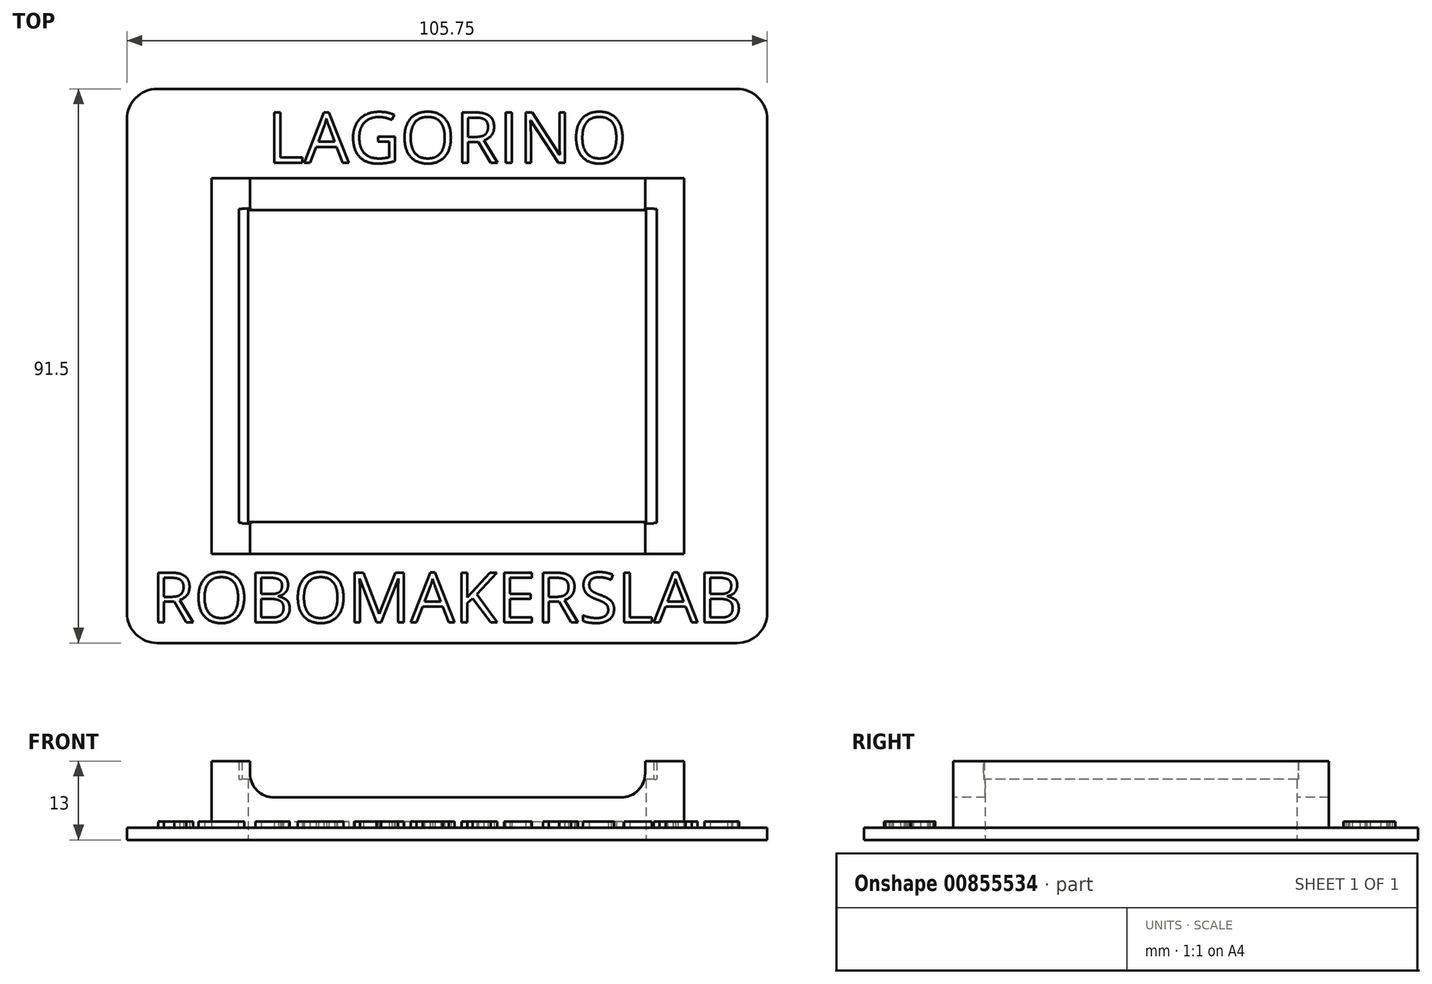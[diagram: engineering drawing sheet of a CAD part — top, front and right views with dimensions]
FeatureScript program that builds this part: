
annotation { "Feature Type Name" : "Feature", "Feature Type Description" : "" }
export const myFeature = defineFeature(function(context is Context, id is Id, definition is map)
    precondition{}
    {
        {
            var Q0;
            Q0=qCreatedBy(makeId("Top.planeOp"),FACE);
            var sketch = newSketch(context, id + "F0", { "sketchPlane" : qUnion([Q0])});
            skLineSegment(sketch, "E0.bottom", {"start": v(-39, 31) * mm, "end": v(39, 31) * mm});
            skLineSegment(sketch, "E0.top", {"start": v(-39, -31) * mm, "end": v(39, -31) * mm});
            skLineSegment(sketch, "E0.left", {"start": v(-39, 31) * mm, "end": v(-39, -31) * mm});
            skLineSegment(sketch, "E0.right", {"start": v(39, 31) * mm, "end": v(39, -31) * mm});
            skPoint(sketch, "E0.middle", {"position": v(0, 0) * mm});
            skLineSegment(sketch, "E1.0", {"start": v(-39, 25.75) * mm, "end": v(39, 25.75) * mm});
            skLineSegment(sketch, "E2.0", {"start": v(-39, -25.75) * mm, "end": v(39, -25.75) * mm});
            skLineSegment(sketch, "E3.0", {"start": v(-33, 31) * mm, "end": v(-33, -31) * mm});
            skLineSegment(sketch, "E4.0", {"start": v(32.75, 31) * mm, "end": v(32.75, -31) * mm});
            skSolve(sketch);
        }
        {
            var Q0;
            Q0 = qSketchRegion(id + "F0", true);
            extrude(context, id + "F1", {"entities" : qUnion([Q0]), "depth" : 10 * mm, "offsetDistance" : 25 * mm});
        }
        {
            var Q0;
            Q0=makeQuery(id+"F1.opExtrude","CAP_FACE",FACE,{"disambiguationData":[OSD([sQuery(id+"F0.wireOp",EDGE,"E0.bottom"),sQuery(id+"F0.wireOp",EDGE,"E0.top"),sQuery(id+"F0.wireOp",EDGE,"E0.left"),sQuery(id+"F0.wireOp",EDGE,"E0.right"),sQuery(id+"F0.wireOp",EDGE,"E1.0"),sQuery(id+"F0.wireOp",EDGE,"E2.0"),sQuery(id+"F0.wireOp",EDGE,"E3.0"),sQuery(id+"F0.wireOp",EDGE,"E4.0")])],"isStart":false});
            var sketch = newSketch(context, id + "F2", { "sketchPlane" : qUnion([Q0])});
            skLineSegment(sketch, "E5.bottom", {"start": v(-39, 31) * mm, "end": v(39, 31) * mm});
            skLineSegment(sketch, "E5.top", {"start": v(-39, -31) * mm, "end": v(39, -31) * mm});
            skLineSegment(sketch, "E5.left", {"start": v(-39, 31) * mm, "end": v(-39, -31) * mm});
            skLineSegment(sketch, "E5.right", {"start": v(39, 31) * mm, "end": v(39, -31) * mm});
            skLineSegment(sketch, "E6.0", {"start": v(-39, 25.9) * mm, "end": v(39, 25.9) * mm});
            skLineSegment(sketch, "E7.0", {"start": v(-39, -25.9) * mm, "end": v(39, -25.9) * mm});
            skLineSegment(sketch, "E8.0", {"start": v(-34.5, 31) * mm, "end": v(-34.5, -31) * mm});
            skLineSegment(sketch, "E9.0", {"start": v(34.5, 31) * mm, "end": v(34.5, -31) * mm});
            skLineSegment(sketch, "E10.0", {"start": v(34, 26) * mm, "end": v(-34, 26) * mm});
            skLineSegment(sketch, "E10.1", {"start": v(34, -26) * mm, "end": v(34, 26) * mm});
            skLineSegment(sketch, "E10.2", {"start": v(-34, -26) * mm, "end": v(34, -26) * mm});
            skLineSegment(sketch, "E10.3", {"start": v(-34, 26) * mm, "end": v(-34, -26) * mm});
            skSolve(sketch);
        }
        {
            var Q0;
            Q0 = qSketchRegion(id + "F2", true);
            extrude(context, id + "F3", {"entities" : qUnion([Q0]), "operationType" : NewBodyOperationType.ADD, "depth" : 3 * mm, "offsetDistance" : 25 * mm});
        }
        {
            var Q0;
            Q0=makeQuery(id+"F3.boolean.opBoolean","MERGE",FACE,{"derivedFrom":[makeQuery(id+"F1.opExtrude","SWEPT_FACE",FACE,{"disambiguationData":[OSD([sQuery(id+"F0.wireOp",EDGE,"E0.top")])]}),makeQuery(id+"F3.opExtrude","SWEPT_FACE",FACE,{"disambiguationData":[OSD([sQuery(id+"F2.wireOp",EDGE,"E5.top")])]})]});
            var sketch = newSketch(context, id + "F4", { "sketchPlane" : qUnion([Q0])});
            skLineSegment(sketch, "E11.bottom", {"start": v(-32.7, 13) * mm, "end": v(32.58, 13) * mm});
            skLineSegment(sketch, "E11.top", {"start": v(-32.7, 7) * mm, "end": v(32.58, 7) * mm});
            skLineSegment(sketch, "E11.left", {"start": v(-32.7, 13) * mm, "end": v(-32.7, 7) * mm});
            skLineSegment(sketch, "E11.right", {"start": v(32.58, 13) * mm, "end": v(32.58, 7) * mm});
            skSolve(sketch);
        }
        {
            var Q0;
            Q0 = qSketchRegion(id + "F4", true);
            extrude(context, id + "F5", {"entities" : qUnion([Q0]), "operationType" : NewBodyOperationType.REMOVE, "oppositeDirection" : true, "depth" : 80 * mm, "offsetDistance" : 25 * mm});
        }
        {
            var Q0;
            {var subQ0=sQuery(id+"F4.wireOp",EDGE,"E11.top");var subQ1=sQuery(id+"F4.wireOp",EDGE,"E11.left");Q0=makeQuery(id+"F5.boolean.opBoolean","COPY",EDGE,{"disambiguationData":[TD([makeQuery(id+"F1.opExtrude","SWEPT_FACE",FACE,{"disambiguationData":[OSD([sQuery(id+"F0.wireOp",EDGE,"E0.top")])]})])],"derivedFrom":makeQuery(id+"F5.opExtrude","SWEPT_EDGE",EDGE,{"disambiguationData":[OSD([subQ0,subQ1])]})});}
            var Q1;
            {var subQ0=sQuery(id+"F4.wireOp",EDGE,"E11.top");var subQ1=sQuery(id+"F4.wireOp",EDGE,"E11.right");Q1=makeQuery(id+"F5.boolean.opBoolean","COPY",EDGE,{"disambiguationData":[TD([makeQuery(id+"F1.opExtrude","SWEPT_FACE",FACE,{"disambiguationData":[OSD([sQuery(id+"F0.wireOp",EDGE,"E0.top")])]})])],"derivedFrom":makeQuery(id+"F5.opExtrude","SWEPT_EDGE",EDGE,{"disambiguationData":[OSD([subQ0,subQ1])]})});}
            var Q2;
            {var subQ0=sQuery(id+"F4.wireOp",EDGE,"E11.top");var subQ1=sQuery(id+"F4.wireOp",EDGE,"E11.left");Q2=makeQuery(id+"F5.boolean.opBoolean","COPY",EDGE,{"disambiguationData":[TD([makeQuery(id+"F1.opExtrude","SWEPT_FACE",FACE,{"disambiguationData":[OSD([sQuery(id+"F0.wireOp",EDGE,"E0.bottom")])]})])],"derivedFrom":makeQuery(id+"F5.opExtrude","SWEPT_EDGE",EDGE,{"disambiguationData":[OSD([subQ0,subQ1])]})});}
            var Q3;
            {var subQ0=sQuery(id+"F4.wireOp",EDGE,"E11.top");var subQ1=sQuery(id+"F4.wireOp",EDGE,"E11.right");Q3=makeQuery(id+"F5.boolean.opBoolean","COPY",EDGE,{"disambiguationData":[TD([makeQuery(id+"F1.opExtrude","SWEPT_FACE",FACE,{"disambiguationData":[OSD([sQuery(id+"F0.wireOp",EDGE,"E0.bottom")])]})])],"derivedFrom":makeQuery(id+"F5.opExtrude","SWEPT_EDGE",EDGE,{"disambiguationData":[OSD([subQ0,subQ1])]})});}
            fillet(context, id + "F6", {"entities" : qUnion([Q0, Q1, Q2, Q3]), "tangentPropagation" : true, "radius" : 4 * mm, "defaultsChanged" : true, "vertexSettings" : [], "allowEdgeOverflow" : false});
        }
        {
            var Q0;
            Q0=makeQuery(id+"F1.opExtrude","CAP_FACE",FACE,{"disambiguationData":[OSD([sQuery(id+"F0.wireOp",EDGE,"E0.bottom"),sQuery(id+"F0.wireOp",EDGE,"E0.top"),sQuery(id+"F0.wireOp",EDGE,"E0.left"),sQuery(id+"F0.wireOp",EDGE,"E0.right"),sQuery(id+"F0.wireOp",EDGE,"E1.0"),sQuery(id+"F0.wireOp",EDGE,"E2.0"),sQuery(id+"F0.wireOp",EDGE,"E3.0"),sQuery(id+"F0.wireOp",EDGE,"E4.0")])],"isStart":true});
            var sketch = newSketch(context, id + "F7", { "sketchPlane" : qUnion([Q0])});
            skLineSegment(sketch, "E12.bottom", {"start": v(-33, 25.75) * mm, "end": v(32.75, 25.75) * mm});
            skLineSegment(sketch, "E12.top", {"start": v(-33, -25.75) * mm, "end": v(32.75, -25.75) * mm});
            skLineSegment(sketch, "E12.left", {"start": v(-33, 25.75) * mm, "end": v(-33, -25.75) * mm});
            skLineSegment(sketch, "E12.right", {"start": v(32.75, 25.75) * mm, "end": v(32.75, -25.75) * mm});
            skLineSegment(sketch, "E13.0", {"start": v(-53, 45.75) * mm, "end": v(52.75, 45.75) * mm});
            skLineSegment(sketch, "E13.1", {"start": v(-53, 45.75) * mm, "end": v(-53, -45.75) * mm});
            skLineSegment(sketch, "E13.2", {"start": v(-53, -45.75) * mm, "end": v(52.75, -45.75) * mm});
            skLineSegment(sketch, "E13.3", {"start": v(52.75, 45.75) * mm, "end": v(52.75, -45.75) * mm});
            skSolve(sketch);
        }
        {
            var Q0;
            Q0 = qSketchRegion(id + "F7", true);
            extrude(context, id + "F8", {"entities" : qUnion([Q0]), "operationType" : NewBodyOperationType.ADD, "oppositeDirection" : true, "depth" : 2 * mm, "offsetDistance" : 25 * mm});
        }
        {
            var Q0;
            Q0=makeQuery(id+"F8.opExtrude","CAP_FACE",FACE,{"disambiguationData":[OSD([sQuery(id+"F7.wireOp",EDGE,"E12.bottom"),sQuery(id+"F7.wireOp",EDGE,"E12.top"),sQuery(id+"F7.wireOp",EDGE,"E12.left"),sQuery(id+"F7.wireOp",EDGE,"E12.right"),sQuery(id+"F7.wireOp",EDGE,"E13.0"),sQuery(id+"F7.wireOp",EDGE,"E13.1"),sQuery(id+"F7.wireOp",EDGE,"E13.2"),sQuery(id+"F7.wireOp",EDGE,"E13.3")])],"isStart":false});
            var sketch = newSketch(context, id + "F9", { "sketchPlane" : qUnion([Q0])});
            skText(sketch, "E14", { "text": "LAGORINO", "fontName": "OpenSans-Regular.ttf"});
            skText(sketch, "E15", { "text": "ROBOMAKERSLAB\n", "fontName": "OpenSans-Regular.ttf"});
            const initialGuessF9  = {"E14": [-0.0298, 0.03353, 1, 0, 0.0084], "E15": [-0.049, -0.04235, 1, 0, 0.00828]};
            skSetInitialGuess(sketch, initialGuessF9);
            skSolve(sketch);
        }
        {
            var Q0;
            Q0 = qSketchRegion(id + "F9", true);
            extrude(context, id + "F10", {"entities" : qUnion([Q0]), "operationType" : NewBodyOperationType.ADD, "depth" : 1 * mm, "offsetDistance" : 25 * mm});
        }
        {
            var Q0;
            Q0=makeQuery(id+"F8.opExtrude","SWEPT_EDGE",EDGE,{"disambiguationData":[OSD([sQuery(id+"F7.wireOp",EDGE,"E13.0"),sQuery(id+"F7.wireOp",EDGE,"E13.1")])]});
            var Q1;
            Q1=makeQuery(id+"F8.opExtrude","SWEPT_EDGE",EDGE,{"disambiguationData":[OSD([sQuery(id+"F7.wireOp",EDGE,"E13.0"),sQuery(id+"F7.wireOp",EDGE,"E13.3")])]});
            var Q2;
            Q2=makeQuery(id+"F8.opExtrude","SWEPT_EDGE",EDGE,{"disambiguationData":[OSD([sQuery(id+"F7.wireOp",EDGE,"E13.2"),sQuery(id+"F7.wireOp",EDGE,"E13.3")])]});
            var Q3;
            Q3=makeQuery(id+"F8.opExtrude","SWEPT_EDGE",EDGE,{"disambiguationData":[OSD([sQuery(id+"F7.wireOp",EDGE,"E13.1"),sQuery(id+"F7.wireOp",EDGE,"E13.2")])]});
            fillet(context, id + "F11", {"entities" : qUnion([Q0, Q1, Q2, Q3]), "tangentPropagation" : true, "radius" : 5 * mm, "defaultsChanged" : false, "vertexSettings" : [], "allowEdgeOverflow" : false});
        }
    });
